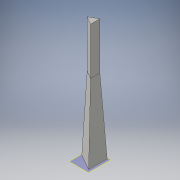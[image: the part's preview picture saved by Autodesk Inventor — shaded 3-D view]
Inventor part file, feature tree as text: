
AUTODESK INVENTOR PART (.ipt)
format: ipt  version: 2016 (Build 200138000, 138)  size: 117,760 bytes
history: native  units: in
note: dims shown in document units (in); Inventor stores cm internally (conversion verified against a paired STEP export)
features: plane x4, split x3, sketch x2, extrude x2
ambient origin geometry x8: Origin, YZ Plane, XZ Plane, XY Plane, X Axis, Y Axis, Z Axis, Center Point
bodies: Body1 (feature_tree)
feature tree (11):
  sketch  "Sketch1"  dims[d10=11.811in d11=11.811in]
  plane  "Work Plane1"
  extrude  "Extrusion2"  Depth=11.811in
  sketch  "Sketch2"  dims[d12=60.0deg d13=5.9055in d14=5.9055in d15=30.0deg d16=48.0in d17=0.0in d18=5.9055in d19=5.9055in d20=30.0in d21=0.0in]
  plane  "Work Plane2"
  split  "Split1"
  plane  "Work Plane3"
  split  "Split2"
  plane  "Work Plane4"
  split  "Split3"
  extrude  "Extrusion3"  Depth=5.9055in
